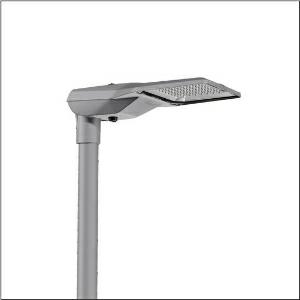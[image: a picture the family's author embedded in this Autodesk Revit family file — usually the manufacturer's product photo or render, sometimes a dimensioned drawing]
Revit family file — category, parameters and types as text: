
# Revit family: streetlight_sl_21_midi___pl52_5xe3h33t08lb_7b8b
name_source: partatom
category: Lighting Fixtures
units: mm (PartAtom-declared; Revit-internal decimal feet)

## family parameters
Cut with Voids When Loaded = No
Host = Face
Light Source = No
Part Type = Normal
Room Calculation Point = No
Round Connector Dimension = Use Diameter
Shared = No

## types (1)
- --- (1 x LED, 14100 lm, 99.6 W, 3000K)
    Apparent Load = 100 VA
    CIE Flux Codes = 27 59 98 100 100
    Color Rendering = 70
    Color Temperature = 3000K
    Default Elevation = 1800 mm
    Description = Streetlight SL 21 midi, mast luminaire, primary light control with lens, of PMMA, primary optical cover: cover, of toughened safety glass, transparent, light distribution: PL52, light emission: direct distribution, primary light characteristic: asymmetric, installation type: side-entry, post-top, LED, High Power LED, rated luminous flux: 14.100lm, luminous efficacy: 142lm/W, light colour: 730, colour temperature: 3000K, control gear: D4i, control: overheat protection, constant luminous flux control, time-dependent luminous flux control, flexible luminous flux parameterisation, pre-setting: logarithmic dimming characteristic, mains connection: 230..240V, AC, 50/60Hz, start of lifetime: 100W, end of service life: 102W, reduction: 46W, luminaire housing, of diecast aluminium, powder-coated, SITECO metallic grey (DB 702S), corrosivity category C5 high according to DIN EN ISO 12944, please order mast flange separately, inclination adjustable: 0°, 5°, 10°, 15°, sealing non-destructively replaceable, multi-level sealing system, length: 644mm, width: 335mm, height: 110mm, mast flange for spigot size: 42mm (side-entry): 5XC10008XM4, 60/48mm (side-entry/post-top): 5XC10108XM2, 76/60mm (side-entry/post-top): 5XC10108XM1, mounting height: 4..8m, Smart Interface below and above, protection rating (complete): IP66, insulation class (complete): insulation class II (safety insulation), certification: CE, ENEC, ENEC+, VDE, impact resistance: IK10, permissible operating ambient temperature for outdoor applications: -40..+50°C, standard-compliant lighting for roads and squares, packaging unit: 1 piece

Light Distribution: PL52
    Height = 111 mm
    Lamp = 1 x LED
    Lamp Light Flux = 14100 lm
    Lamp Power = 99.6 W
    Lamp count = 1
    Length = 644 mm
    Luminous efficacy = 142 lm/W
    Manufacturer = Siteco
    ModVariant = No
    Model = 5XE3H33T08LB
    Number of Poles = 1
    OnlyDefault = Yes
    Power Factor = 1
    Product Name = Streetlight SL 21 midi | PL52
    Product group = mast luminaire | pylon top
    ProductGroupID = 6100
    Protection Class = Protection class II
    Protection Degree = IP 66
    RLX_Detail_Level = 1
    RLX_Emergency_Light_Flux = 0 lm
    RLX_Emergency_Type = 0
    RLX_Emergency_Type_DB = No
    RlxData = <blob elided: 36529 chars, md5=48254b72>
    Socket = socket
    Standby Power = 0 W
    System Light Flux = 14100 lm
    System Power = 100 W
    Type Comments = factory setting: luminous flux: 100 % | dim-lin: 254 | 1020 mA
    Type Image = l_1004304.jpg
    URL = http://relux.com
    VarID = @adj_032147
    Voltage = 0 V
    Weight = 0.00 kg
    Width = 336 mm

## geometry (parser evidence)
native form markers: Blend x4, Sweep x10
no freeform markers — native parametric forms only
